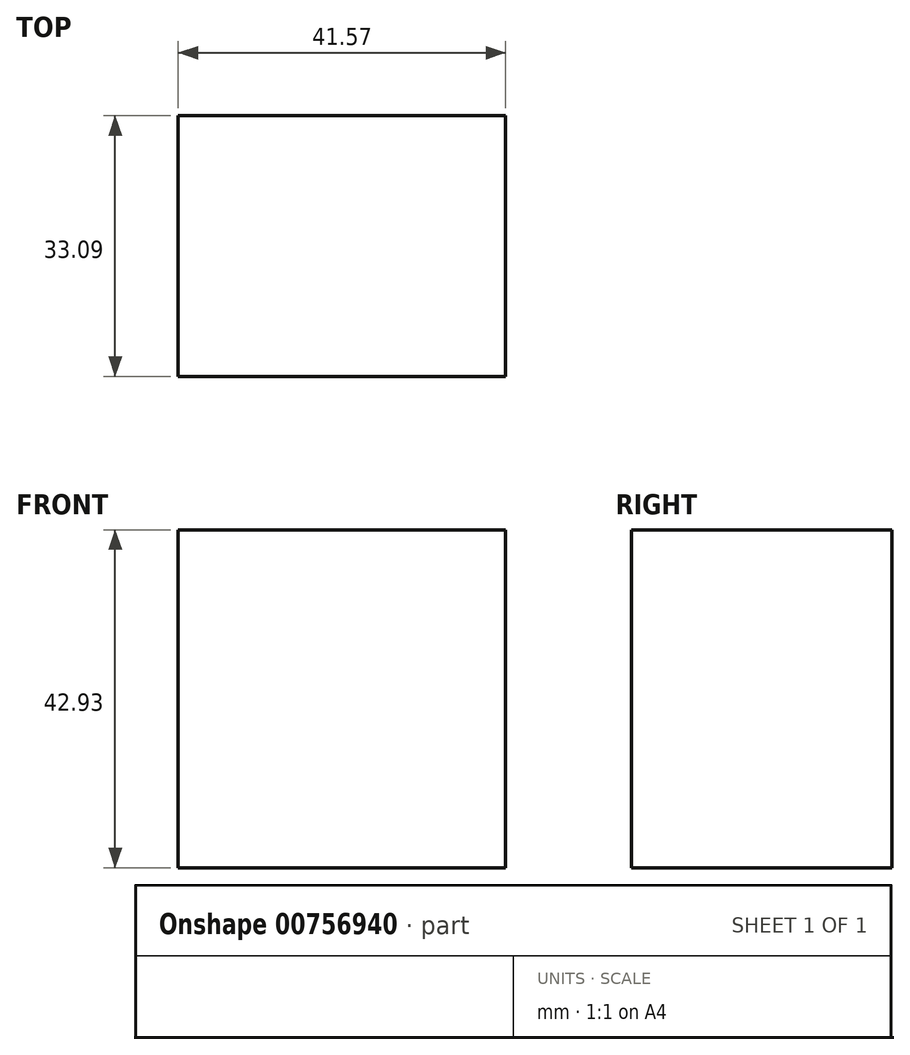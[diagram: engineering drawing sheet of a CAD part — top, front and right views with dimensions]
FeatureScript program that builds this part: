
annotation { "Feature Type Name" : "Feature", "Feature Type Description" : "" }
export const myFeature = defineFeature(function(context is Context, id is Id, definition is map)
    precondition{}
    {
        {
            var Q0;
            Q0=qCreatedBy(makeId("Top.planeOp"),FACE);
            var sketch = newSketch(context, id + "F0", { "sketchPlane" : qUnion([Q0])});
            skLineSegment(sketch, "E0", {"start": v(0, 0) * mm, "end": v(41.57, 0) * mm});
            skLineSegment(sketch, "E1", {"start": v(41.57, 0) * mm, "end": v(41.57, -33.1) * mm});
            skLineSegment(sketch, "E2", {"start": v(41.57, -33.1) * mm, "end": v(0, -33.1) * mm});
            skLineSegment(sketch, "E3", {"start": v(0, -33.1) * mm, "end": v(0, 0) * mm});
            skSolve(sketch);
        }
        {
            var Q0;
            Q0=makeQuery(id+"F0.imprint","IMPRINT",FACE,{"disambiguationData":[TD([[makeQuery(id+"F0.imprint","IMPRINT",EDGE,{"derivedFrom":sQuery(id+"F0.wireOp",EDGE,"E0")}),-1.0]])]});
            extrude(context, id + "F1", {"entities" : qUnion([Q0]), "depth" : 42.93 * mm, "offsetDistance" : 25.4 * mm});
        }
    });
